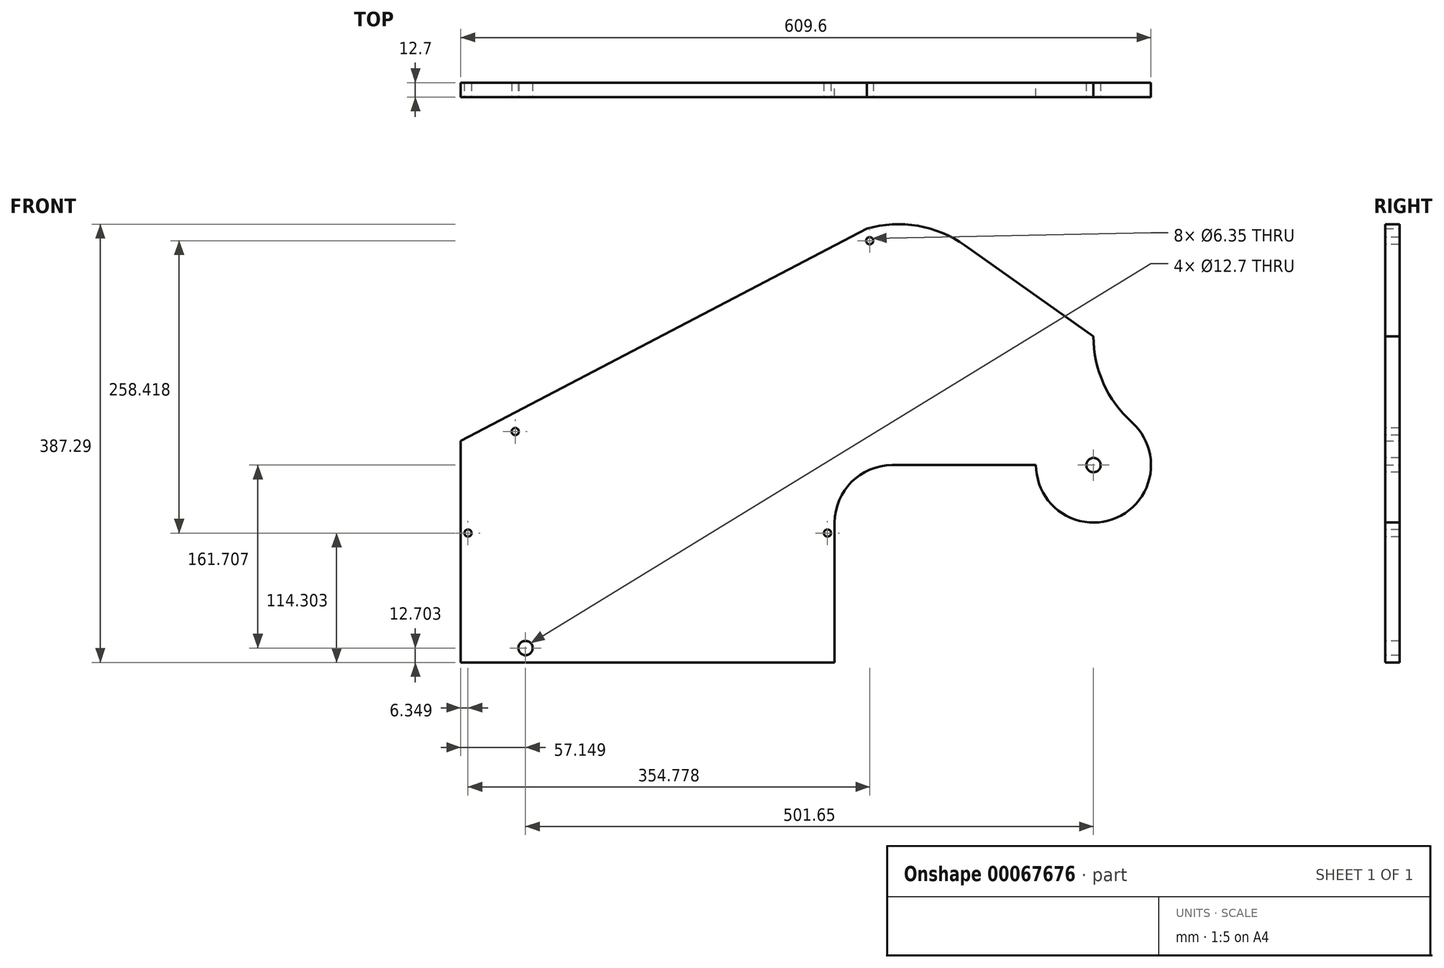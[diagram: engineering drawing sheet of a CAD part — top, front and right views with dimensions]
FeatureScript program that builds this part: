
annotation { "Feature Type Name" : "Feature", "Feature Type Description" : "" }
export const myFeature = defineFeature(function(context is Context, id is Id, definition is map)
    precondition{}
    {
        {
            var Q0;
            Q0=qCreatedBy(makeId("Front.planeOp"),FACE);
            var sketch = newSketch(context, id + "F0", { "sketchPlane" : qUnion([Q0])});
            skLineSegment(sketch, "E0.top", {"start": v(-326.1, -204.06) * mm, "end": v(4.1, -204.06) * mm});
            skLineSegment(sketch, "E0.left", {"start": v(-326.1, -8.11) * mm, "end": v(-326.1, -204.06) * mm});
            skLineSegment(sketch, "E0.right", {"start": v(4.1, -80.45) * mm, "end": v(4.1, -204.06) * mm});
            skLineSegment(sketch, "E1.top", {"start": v(54.9, -29.65) * mm, "end": v(181.9, -29.65) * mm});
            skArc(sketch, "E2", {"start": v(181.9, -29.65) * mm, "mid": v(253.44, -76.02) * mm, "end": v(266.57, 8.21) * mm});
            skPoint(sketch, "E3.visualSharp", {"position": v(232.7, 21.15) * mm});
            skArc(sketch, "E3.filletArc", {"start": v(232.7, 84.12) * mm, "mid": v(241.51, 42.55) * mm, "end": v(266.57, 8.21) * mm});
            skLineSegment(sketch, "E4", {"start": v(232.7, 84.12) * mm, "end": v(119.22, 164.53) * mm});
            skPoint(sketch, "E5.visualSharp", {"position": v(80.5, 191.96) * mm});
            skArc(sketch, "E5.filletArc", {"start": v(119.22, 164.53) * mm, "mid": v(77.53, 181.79) * mm, "end": v(32.49, 179.3) * mm});
            skPoint(sketch, "E6.visualSharp", {"position": v(-326.1, -0.86) * mm});
            skPoint(sketch, "E7.visualSharp", {"position": v(4.1, -29.65) * mm});
            skArc(sketch, "E7.filletArc", {"start": v(54.9, -29.65) * mm, "mid": v(18.98, -44.53) * mm, "end": v(4.1, -80.45) * mm});
            skLineSegment(sketch, "E8", {"start": v(-326.1, -8.11) * mm, "end": v(32.49, 179.3) * mm});
            skSolve(sketch);
        }
        {
            var Q0;
            Q0=makeQuery(id+"F0.imprint","IMPRINT",FACE,{"disambiguationData":[TD([[makeQuery(id+"F0.imprint","IMPRINT",EDGE,{"derivedFrom":sQuery(id+"F0.wireOp",EDGE,"E0.top")}),1.0]])]});
            extrude(context, id + "F1", {"entities" : qUnion([Q0]), "depth" : 12.7 * mm});
        }
        {
            var Q0;
            Q0=makeQuery(id+"F1.opExtrude","CAP_FACE",FACE,{"disambiguationData":[OSD([sQuery(id+"F0.wireOp",EDGE,"E0.top"),sQuery(id+"F0.wireOp",EDGE,"E0.left"),sQuery(id+"F0.wireOp",EDGE,"E0.right"),sQuery(id+"F0.wireOp",EDGE,"E1.top"),sQuery(id+"F0.wireOp",EDGE,"baa10477-8654-412b-942c-05d38897cedc"),sQuery(id+"F0.wireOp",EDGE,"E2"),sQuery(id+"F0.wireOp",EDGE,"E3.filletArc"),sQuery(id+"F0.wireOp",EDGE,"E4"),sQuery(id+"F0.wireOp",EDGE,"E5.filletArc"),sQuery(id+"F0.wireOp",EDGE,"E6.filletArc"),sQuery(id+"F0.wireOp",EDGE,"E7.filletArc")])],"isStart":false});
            var sketch = newSketch(context, id + "F2", { "sketchPlane" : qUnion([Q0])});
            skPoint(sketch, "E9", {"position": v(232.7, -29.65) * mm});
            skPoint(sketch, "E10", {"position": v(-268.95, -191.36) * mm});
            skSolve(sketch);
        }
        {
            var Q0;
            Q0=sQuery(id+"F2.wireOp",VERTEX,"E9");
            var Q1;
            Q1=sQuery(id+"F2.wireOp",VERTEX,"E10");
            var Q2;
            Q2=makeQuery(id+"F1.opExtrude","SWEPT_BODY",BODY,{"disambiguationData":[OSD([sQuery(id+"F0.wireOp",EDGE,"E0.top"),sQuery(id+"F0.wireOp",EDGE,"E0.left"),sQuery(id+"F0.wireOp",EDGE,"E0.right"),sQuery(id+"F0.wireOp",EDGE,"E1.top"),sQuery(id+"F0.wireOp",EDGE,"baa10477-8654-412b-942c-05d38897cedc"),sQuery(id+"F0.wireOp",EDGE,"E2"),sQuery(id+"F0.wireOp",EDGE,"E3.filletArc"),sQuery(id+"F0.wireOp",EDGE,"E4"),sQuery(id+"F0.wireOp",EDGE,"E5.filletArc"),sQuery(id+"F0.wireOp",EDGE,"E6.filletArc"),sQuery(id+"F0.wireOp",EDGE,"E7.filletArc")])]});
            hole(context, id + "F3", {"style" : HoleStyle.SIMPLE, "holeDiameter" : 12.7 * mm, "endStyle" : HoleEndStyle.THROUGH, "locations" : qUnion([Q0, Q1]), "scope" : qUnion([Q2])});
        }
        {
            var Q0;
            Q0=makeQuery(id+"F1.opExtrude","CAP_FACE",FACE,{"disambiguationData":[OSD([sQuery(id+"F0.wireOp",EDGE,"E0.top"),sQuery(id+"F0.wireOp",EDGE,"E0.left"),sQuery(id+"F0.wireOp",EDGE,"E0.right"),sQuery(id+"F0.wireOp",EDGE,"E1.top"),sQuery(id+"F0.wireOp",EDGE,"baa10477-8654-412b-942c-05d38897cedc"),sQuery(id+"F0.wireOp",EDGE,"E2"),sQuery(id+"F0.wireOp",EDGE,"E3.filletArc"),sQuery(id+"F0.wireOp",EDGE,"E4"),sQuery(id+"F0.wireOp",EDGE,"E5.filletArc"),sQuery(id+"F0.wireOp",EDGE,"E6.filletArc"),sQuery(id+"F0.wireOp",EDGE,"E7.filletArc")])],"isStart":false});
            var sketch = newSketch(context, id + "F4", { "sketchPlane" : qUnion([Q0])});
            skPoint(sketch, "E11", {"position": v(-319.75, -89.76) * mm});
            skSolve(sketch);
        }
        {
            var Q0;
            Q0=sQuery(id+"F4.wireOp",VERTEX,"E11");
            var Q1;
            Q1=makeQuery(id+"F1.opExtrude","SWEPT_BODY",BODY,{"disambiguationData":[OSD([sQuery(id+"F0.wireOp",EDGE,"E0.top"),sQuery(id+"F0.wireOp",EDGE,"E0.left"),sQuery(id+"F0.wireOp",EDGE,"E0.right"),sQuery(id+"F0.wireOp",EDGE,"E1.top"),sQuery(id+"F0.wireOp",EDGE,"baa10477-8654-412b-942c-05d38897cedc"),sQuery(id+"F0.wireOp",EDGE,"E2"),sQuery(id+"F0.wireOp",EDGE,"E3.filletArc"),sQuery(id+"F0.wireOp",EDGE,"E4"),sQuery(id+"F0.wireOp",EDGE,"E5.filletArc"),sQuery(id+"F0.wireOp",EDGE,"E6.filletArc"),sQuery(id+"F0.wireOp",EDGE,"E7.filletArc")])]});
            hole(context, id + "F5", {"style" : HoleStyle.SIMPLE, "holeDiameter" : 6.35 * mm, "endStyle" : HoleEndStyle.THROUGH, "locations" : qUnion([Q0]), "scope" : qUnion([Q1])});
        }
        {
            var Q0;
            Q0=makeQuery(id+"F1.opExtrude","CAP_FACE",FACE,{"disambiguationData":[OSD([sQuery(id+"F0.wireOp",EDGE,"E0.top"),sQuery(id+"F0.wireOp",EDGE,"E0.left"),sQuery(id+"F0.wireOp",EDGE,"E0.right"),sQuery(id+"F0.wireOp",EDGE,"E1.top"),sQuery(id+"F0.wireOp",EDGE,"baa10477-8654-412b-942c-05d38897cedc"),sQuery(id+"F0.wireOp",EDGE,"E2"),sQuery(id+"F0.wireOp",EDGE,"E3.filletArc"),sQuery(id+"F0.wireOp",EDGE,"E4"),sQuery(id+"F0.wireOp",EDGE,"E5.filletArc"),sQuery(id+"F0.wireOp",EDGE,"E6.filletArc"),sQuery(id+"F0.wireOp",EDGE,"E7.filletArc")])],"isStart":false});
            var sketch = newSketch(context, id + "F6", { "sketchPlane" : qUnion([Q0])});
            skPoint(sketch, "E12", {"position": v(-2.25, -89.76) * mm});
            skSolve(sketch);
        }
        {
            var Q0;
            Q0=sQuery(id+"F6.wireOp",VERTEX,"E12");
            var Q1;
            Q1=makeQuery(id+"F1.opExtrude","SWEPT_BODY",BODY,{"disambiguationData":[OSD([sQuery(id+"F0.wireOp",EDGE,"E0.top"),sQuery(id+"F0.wireOp",EDGE,"E0.left"),sQuery(id+"F0.wireOp",EDGE,"E0.right"),sQuery(id+"F0.wireOp",EDGE,"E1.top"),sQuery(id+"F0.wireOp",EDGE,"baa10477-8654-412b-942c-05d38897cedc"),sQuery(id+"F0.wireOp",EDGE,"E2"),sQuery(id+"F0.wireOp",EDGE,"E3.filletArc"),sQuery(id+"F0.wireOp",EDGE,"E4"),sQuery(id+"F0.wireOp",EDGE,"E5.filletArc"),sQuery(id+"F0.wireOp",EDGE,"E6.filletArc"),sQuery(id+"F0.wireOp",EDGE,"E7.filletArc")])]});
            hole(context, id + "F7", {"style" : HoleStyle.SIMPLE, "holeDiameter" : 6.35 * mm, "endStyle" : HoleEndStyle.THROUGH, "locations" : qUnion([Q0]), "scope" : qUnion([Q1])});
        }
        {
            var Q0;
            Q0=makeQuery(id+"F1.opExtrude","CAP_FACE",FACE,{"disambiguationData":[OSD([sQuery(id+"F0.wireOp",EDGE,"E0.top"),sQuery(id+"F0.wireOp",EDGE,"E0.left"),sQuery(id+"F0.wireOp",EDGE,"E0.right"),sQuery(id+"F0.wireOp",EDGE,"E1.top"),sQuery(id+"F0.wireOp",EDGE,"baa10477-8654-412b-942c-05d38897cedc"),sQuery(id+"F0.wireOp",EDGE,"E2"),sQuery(id+"F0.wireOp",EDGE,"E3.filletArc"),sQuery(id+"F0.wireOp",EDGE,"E4"),sQuery(id+"F0.wireOp",EDGE,"E5.filletArc"),sQuery(id+"F0.wireOp",EDGE,"E6.filletArc"),sQuery(id+"F0.wireOp",EDGE,"E7.filletArc")])],"isStart":false});
            var sketch = newSketch(context, id + "F8", { "sketchPlane" : qUnion([Q0])});
            skPoint(sketch, "E13", {"position": v(35.03, 168.66) * mm});
            skPoint(sketch, "E14", {"position": v(25.58, 177.15) * mm});
            skSolve(sketch);
        }
        {
            var Q0;
            Q0=sQuery(id+"F8.wireOp",VERTEX,"E13");
            var Q1;
            Q1=makeQuery(id+"F1.opExtrude","SWEPT_BODY",BODY,{"disambiguationData":[OSD([sQuery(id+"F0.wireOp",EDGE,"E0.top"),sQuery(id+"F0.wireOp",EDGE,"E0.left"),sQuery(id+"F0.wireOp",EDGE,"E0.right"),sQuery(id+"F0.wireOp",EDGE,"E1.top"),sQuery(id+"F0.wireOp",EDGE,"baa10477-8654-412b-942c-05d38897cedc"),sQuery(id+"F0.wireOp",EDGE,"E2"),sQuery(id+"F0.wireOp",EDGE,"E3.filletArc"),sQuery(id+"F0.wireOp",EDGE,"E4"),sQuery(id+"F0.wireOp",EDGE,"E5.filletArc"),sQuery(id+"F0.wireOp",EDGE,"E6.filletArc"),sQuery(id+"F0.wireOp",EDGE,"E7.filletArc")])]});
            hole(context, id + "F9", {"style" : HoleStyle.SIMPLE, "holeDiameter" : 6.35 * mm, "endStyle" : HoleEndStyle.THROUGH, "locations" : qUnion([Q0]), "scope" : qUnion([Q1])});
        }
        {
            var Q0;
            Q0=makeQuery(id+"F1.opExtrude","CAP_FACE",FACE,{"disambiguationData":[OSD([sQuery(id+"F0.wireOp",EDGE,"E0.top"),sQuery(id+"F0.wireOp",EDGE,"E0.left"),sQuery(id+"F0.wireOp",EDGE,"E0.right"),sQuery(id+"F0.wireOp",EDGE,"E1.top"),sQuery(id+"F0.wireOp",EDGE,"baa10477-8654-412b-942c-05d38897cedc"),sQuery(id+"F0.wireOp",EDGE,"E2"),sQuery(id+"F0.wireOp",EDGE,"E3.filletArc"),sQuery(id+"F0.wireOp",EDGE,"E4"),sQuery(id+"F0.wireOp",EDGE,"E5.filletArc"),sQuery(id+"F0.wireOp",EDGE,"E6.filletArc"),sQuery(id+"F0.wireOp",EDGE,"E7.filletArc")])],"isStart":false});
            var sketch = newSketch(context, id + "F10", { "sketchPlane" : qUnion([Q0])});
            skPoint(sketch, "E15", {"position": v(-278.06, 0) * mm});
            skLineSegment(sketch, "E16", {"start": v(35.03, 168.66) * mm, "end": v(-278.06, 0.05) * mm});
            skSolve(sketch);
        }
        {
            var Q0;
            Q0=sQuery(id+"F10.wireOp",VERTEX,"E15");
            var Q1;
            Q1=makeQuery(id+"F1.opExtrude","SWEPT_BODY",BODY,{"disambiguationData":[OSD([sQuery(id+"F0.wireOp",EDGE,"E0.top"),sQuery(id+"F0.wireOp",EDGE,"E0.left"),sQuery(id+"F0.wireOp",EDGE,"E0.right"),sQuery(id+"F0.wireOp",EDGE,"E1.top"),sQuery(id+"F0.wireOp",EDGE,"baa10477-8654-412b-942c-05d38897cedc"),sQuery(id+"F0.wireOp",EDGE,"E2"),sQuery(id+"F0.wireOp",EDGE,"E3.filletArc"),sQuery(id+"F0.wireOp",EDGE,"E4"),sQuery(id+"F0.wireOp",EDGE,"E5.filletArc"),sQuery(id+"F0.wireOp",EDGE,"E6.filletArc"),sQuery(id+"F0.wireOp",EDGE,"E7.filletArc")])]});
            hole(context, id + "F11", {"style" : HoleStyle.SIMPLE, "holeDiameter" : 6.35 * mm, "endStyle" : HoleEndStyle.THROUGH, "locations" : qUnion([Q0]), "scope" : qUnion([Q1])});
        }
    });
